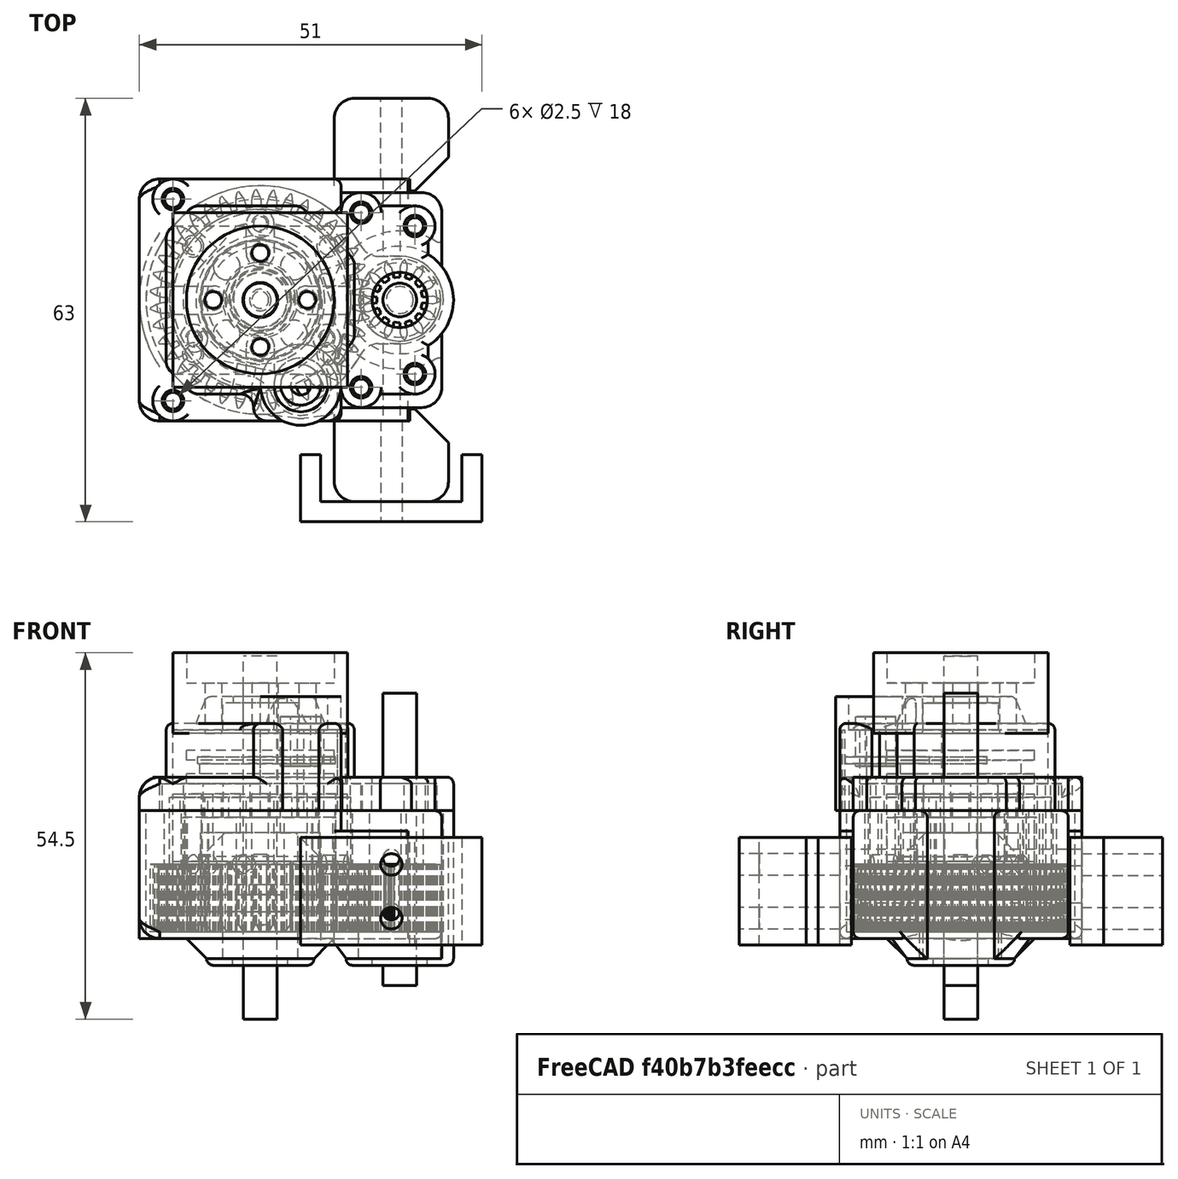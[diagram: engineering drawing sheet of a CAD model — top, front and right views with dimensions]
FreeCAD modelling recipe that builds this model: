
FCSTD DOCUMENT  (FreeCAD 0.16R6348 (Git))
Label: transfer-case
License: All rights reserved
LicenseURL: http://en.wikipedia.org/wiki/All_rights_reserved
objects: Part::Cylinder×134, Part::MultiFuse×79, Part::Feature×69, Part::Cut×42, Part::Box×25, Part::Fillet×23, Part::Chamfer×11, Part::Extrusion×3, Part::Mirroring×2, Part::Cone×2, Part::Part2DObjectPython×1, Part::Fuse×1, Part::FeaturePython×1
note: 393 computed .brp shape members not serialized (recipe doc carries the construction recipe); baked Part::Feature solids carry a one-line shape summary decoded from their .brp

FEATURE [Part::Cylinder] Cylinder
  Angle = 60
  Height = 7
  Placement = pos=(0,0,0) rot=(0,0,-1;0.20944rad)
  Radius = 11.5
FEATURE [Part::Cylinder] Cylinder001
  Angle = 60
  Height = 7
  Placement = pos=(0,0,0) rot=(0,0,1;3.97935rad)
  Radius = 11.5
FEATURE [Part::Cylinder] Cylinder002
  Angle = 60
  Height = 7
  Placement = pos=(0,0,0) rot=(0,0,1;1.88496rad)
  Radius = 11.5
FEATURE [Part::MultiFuse] Fusion
  Shapes = -> [Cylinder,Cylinder001,Cylinder002]
FEATURE [Part::Cylinder] Cylinder009
  Angle = 360
  Height = 10
  Placement = pos=(0,0,0) rot=(0,0,-1;0.20944rad)
  Radius = 13.5
FEATURE [Part::Cylinder] Cylinder010
  Angle = 360
  Height = 7
  Placement = pos=(0,0,0) rot=(0,0,-1;0.20944rad)
  Radius = 11.5
FEATURE [Part::Feature] Face
  shape: bbox 33.81 x 33.81 x 2e-07 mm, 1 faces, 0 solids (baked)
FEATURE [Part::Extrusion] Extrude
  Base = -> Face
  Dir = (0,0,7)
  Solid = false
FEATURE [Part::Cut] Cut
  Base = -> Fusion
  Tool = -> Extrude
FEATURE [Part::Cut] Cut001
  Base = -> Cylinder009
  Tool = -> Cylinder010
FEATURE [Part::Cylinder] Cylinder017
  Angle = 360
  Height = 20
  Radius = 4.7
FEATURE [Part::Cylinder] Cylinder018
  Angle = 360
  Height = 20
  Placement = pos=(0,0,-9) rot=(0,0,1;0rad)
  Radius = 1.4
FEATURE [Part::Cylinder] Cylinder019
  Angle = 360
  Height = 20
  Placement = pos=(0,0,-9) rot=(0,-1,0;2.0944rad)
  Radius = 1.4
FEATURE [Part::Cylinder] Cylinder020
  Angle = 360
  Height = 20
  Placement = pos=(0,0,-9) rot=(0,1,0;2.0944rad)
  Radius = 1.4
FEATURE [Part::MultiFuse] Fusion004
  Placement = pos=(-1.87121,-8.80333,0) rot=(0.989133,-0.103962,-0.103962;1.58172rad)
  Shapes = -> [Cylinder018,Cylinder019,Cylinder020]
FEATURE [Part::MultiFuse] Fusion005
  Shapes = -> [Cut,Cut001]
FEATURE [Part::Cut] Cut002
  Base = -> Fusion005
  Tool = -> Fusion004
FEATURE [Part::Cut] Cut003  label="hemi-box-01"
  Base = -> Cut002
  Tool = -> Cylinder017
FEATURE [Part::Cylinder] Cylinder021
  Angle = 360
  Height = 20
  Radius = 4.7
FEATURE [Part::Feature] Face001
  shape: bbox 33.81 x 33.81 x 2e-07 mm, 1 faces, 0 solids (baked)
FEATURE [Part::Extrusion] Extrude001
  Base = -> Face001
  Dir = (0,0,7)
  Solid = false
FEATURE [Part::Cylinder] Cylinder022
  Angle = 360
  Height = 20
  Placement = pos=(0,0,-9) rot=(0,0,1;0rad)
  Radius = 1.4
FEATURE [Part::Cylinder] Cylinder023
  Angle = 60
  Height = 7
  Placement = pos=(0,0,0) rot=(0,0,1;3.97935rad)
  Radius = 11.5
FEATURE [Part::Cylinder] Cylinder024
  Angle = 60
  Height = 7
  Placement = pos=(0,0,0) rot=(0,0,1;1.88496rad)
  Radius = 11.5
FEATURE [Part::Cylinder] Cylinder025
  Angle = 60
  Height = 7
  Placement = pos=(0,0,0) rot=(0,0,-1;0.20944rad)
  Radius = 11.5
FEATURE [Part::MultiFuse] Fusion007
  Shapes = -> [Cylinder025,Cylinder023,Cylinder024]
FEATURE [Part::Cut] Cut005
  Base = -> Fusion007
  Tool = -> Extrude001
FEATURE [Part::Cylinder] Cylinder026
  Angle = 360
  Height = 10
  Placement = pos=(0,0,0) rot=(0,0,-1;0.20944rad)
  Radius = 13.5
FEATURE [Part::Cylinder] Cylinder027
  Angle = 360
  Height = 7
  Placement = pos=(0,0,0) rot=(0,0,-1;0.20944rad)
  Radius = 11.5
FEATURE [Part::Cut] Cut006
  Base = -> Cylinder026
  Tool = -> Cylinder027
FEATURE [Part::MultiFuse] Fusion008
  Shapes = -> [Cut005,Cut006]
FEATURE [Part::Cylinder] Cylinder028
  Angle = 360
  Height = 20
  Placement = pos=(0,0,-9) rot=(0,-1,0;2.0944rad)
  Radius = 1.4
FEATURE [Part::Cylinder] Cylinder029
  Angle = 360
  Height = 20
  Placement = pos=(0,0,-9) rot=(0,1,0;2.0944rad)
  Radius = 1.4
FEATURE [Part::MultiFuse] Fusion006
  Placement = pos=(-1.87121,-8.80333,0) rot=(0.989133,-0.103962,-0.103962;1.58172rad)
  Shapes = -> [Cylinder022,Cylinder028,Cylinder029]
FEATURE [Part::Cut] Cut007
  Base = -> Fusion008
  Tool = -> Fusion006
FEATURE [Part::Cut] Cut004  label="hemi-box-01-copy"
  Base = -> Cut007
  Tool = -> Cylinder021
FEATURE [Part::Mirroring] Part__Mirroring  label="hemi-box-02"
  Base = (0,0,0)
  Normal = (0,0,1)
  Source = -> Cut004
FEATURE [Part::Feature] Cut014001  label="Cut015"
  Placement = pos=(0,0,-10) rot=(0,0,1;0rad)
  shape: bbox 32.76 x 32.78 x 10 mm, 549 faces (baked)
FEATURE [Part::Cylinder] Cylinder037
  Angle = 360
  Height = 10
  Placement = pos=(8.47185,-7.62809,0) rot=(0,0,-1;0.733038rad)
  Radius = 2.05
FEATURE [Part::Cylinder] Cylinder038
  Angle = 360
  Height = 10
  Placement = pos=(-10.842,-3.52279,0) rot=(0,0,1;3.45575rad)
  Radius = 2.05
FEATURE [Part::Cylinder] Cylinder039
  Angle = 360
  Height = 10
  Placement = pos=(2.37019,11.1509,0) rot=(0,0,1;1.36136rad)
  Radius = 2.05
FEATURE [Part::MultiFuse] Fusion014
  Placement = pos=(0,0,-10) rot=(0,0,1;0.20944rad)
  Shapes = -> [Cylinder037,Cylinder039,Cylinder038]
FEATURE [Part::Cylinder] Cylinder040
  Angle = 360
  Height = 10
  Placement = pos=(8.47185,-7.62809,0) rot=(0,0,-1;0.733038rad)
  Radius = 1.25
FEATURE [Part::Cylinder] Cylinder041
  Angle = 360
  Height = 10
  Placement = pos=(-10.842,-3.52279,0) rot=(0,0,1;3.45575rad)
  Radius = 1.25
FEATURE [Part::Cylinder] Cylinder042
  Angle = 360
  Height = 10
  Placement = pos=(2.37019,11.1509,0) rot=(0,0,1;1.36136rad)
  Radius = 1.25
FEATURE [Part::MultiFuse] Fusion015
  Placement = pos=(0,0,0) rot=(0,0,1;0.20944rad)
  Shapes = -> [Cylinder040,Cylinder042,Cylinder041]
FEATURE [Part::Cylinder] Cylinder043
  Angle = 360
  Height = 10
  Placement = pos=(8.47185,-7.62809,0) rot=(0,0,-1;0.733038rad)
  Radius = 2.05
FEATURE [Part::Cylinder] Cylinder044
  Angle = 360
  Height = 10
  Placement = pos=(-10.842,-3.52279,0) rot=(0,0,1;3.45575rad)
  Radius = 2.05
FEATURE [Part::Cylinder] Cylinder045
  Angle = 360
  Height = 10
  Placement = pos=(2.37019,11.1509,0) rot=(0,0,1;1.36136rad)
  Radius = 2.05
FEATURE [Part::MultiFuse] Fusion017
  Placement = pos=(0,0,0) rot=(0,0,1;0.20944rad)
  Shapes = -> [Cylinder043,Cylinder045,Cylinder044]
FEATURE [Part::Cylinder] Cylinder049
  Angle = 360
  Height = 10
  Placement = pos=(2.37019,11.1509,0) rot=(0,0,1;1.36136rad)
  Radius = 1
FEATURE [Part::Cylinder] Cylinder050
  Angle = 360
  Height = 10
  Placement = pos=(8.47185,-7.62809,0) rot=(0,0,-1;0.733038rad)
  Radius = 1
FEATURE [Part::Cylinder] Cylinder051
  Angle = 360
  Height = 10
  Placement = pos=(-10.842,-3.52279,0) rot=(0,0,1;3.45575rad)
  Radius = 1
FEATURE [Part::MultiFuse] Fusion020
  Placement = pos=(0,0,-9) rot=(0,0,1;0.20944rad)
  Shapes = -> [Cylinder050,Cylinder049,Cylinder051]
FEATURE [Part::MultiFuse] Fusion021
  Shapes = -> [Cut003,Fusion017]
FEATURE [Part::MultiFuse] Fusion022
  Shapes = -> [Fusion014,Part__Mirroring]
FEATURE [Part::MultiFuse] Fusion023
  Shapes = -> [Cut014001,Fusion022]
FEATURE [Part::Cut] Cut014008  label="diff-box-geared"
  Base = -> Fusion023
  Placement = pos=(0,0,-0.5) rot=(0,0,1;0rad)
  Tool = -> Fusion020
FEATURE [Part::Cylinder] Cylinder062
  Angle = 360
  Height = 2
  Placement = pos=(8.47185,-7.62809,0) rot=(0,0,-1;0.733038rad)
  Radius = 2.05
FEATURE [Part::Cylinder] Cylinder063
  Angle = 360
  Height = 2
  Placement = pos=(-10.842,-3.52279,0) rot=(0,0,1;3.45575rad)
  Radius = 2.05
FEATURE [Part::Cylinder] Cylinder064
  Angle = 360
  Height = 2
  Placement = pos=(2.37019,11.1509,0) rot=(0,0,1;1.36136rad)
  Radius = 2.05
FEATURE [Part::MultiFuse] Fusion030
  Placement = pos=(0,0,8) rot=(0,0,1;0.20944rad)
  Shapes = -> [Cylinder062,Cylinder064,Cylinder063]
FEATURE [Part::MultiFuse] Fusion031
  Shapes = -> [Fusion015,Fusion030]
FEATURE [Part::Cylinder] Cylinder065
  Angle = 360
  Height = 10
  Placement = pos=(7,0,0) rot=(0,0,1;0rad)
  Radius = 1.25
FEATURE [Part::Cylinder] Cylinder066
  Angle = 360
  Height = 10
  Placement = pos=(-7,0,0) rot=(0,0,1;0rad)
  Radius = 1.25
FEATURE [Part::MultiFuse] Fusion032
  Shapes = -> [Cylinder066,Cylinder065]
FEATURE [Part::Cylinder] Cylinder067
  Angle = 360
  Height = 10
  Placement = pos=(7,0,0) rot=(0,0,1;0rad)
  Radius = 1.25
FEATURE [Part::Cylinder] Cylinder068
  Angle = 360
  Height = 10
  Placement = pos=(-7,0,0) rot=(0,0,1;0rad)
  Radius = 1.25
FEATURE [Part::MultiFuse] Fusion033
  Placement = pos=(0,0,0) rot=(0,0,1;1.5708rad)
  Shapes = -> [Cylinder068,Cylinder067]
FEATURE [Part::MultiFuse] Fusion034
  Shapes = -> [Fusion033,Fusion032]
FEATURE [Part::Cut] Cut014009
  Base = -> Fusion021
  Tool = -> Fusion031
FEATURE [Part::Cut] Cut014010  label="diff-box-ungeared"
  Base = -> Cut014009
  Placement = pos=(0,0,-0.5) rot=(0,0,1;0rad)
  Tool = -> Fusion034
FEATURE [Part::Cylinder] Cylinder070
  Angle = 360
  Height = 4.2
  Radius = 8.9
FEATURE [Part::Cylinder] Cylinder072
  Angle = 360
  Height = 12
  Radius = 1.25
FEATURE [Part::MultiFuse] Fusion036
  Shapes = -> [Cylinder072,Cylinder070]
FEATURE [Part::Cylinder] Cylinder073
  Angle = 360
  Height = 15
  Placement = pos=(7,0,0) rot=(0,0,1;0rad)
  Radius = 2.1
FEATURE [Part::Cylinder] Cylinder074
  Angle = 360
  Height = 15
  Placement = pos=(-7,0,0) rot=(0,0,1;0rad)
  Radius = 2.1
FEATURE [Part::MultiFuse] Fusion037
  Shapes = -> [Cylinder074,Cylinder073]
FEATURE [Part::Cylinder] Cylinder075
  Angle = 360
  Height = 15
  Placement = pos=(7,0,0) rot=(0,0,1;0rad)
  Radius = 2.1
FEATURE [Part::Cylinder] Cylinder076
  Angle = 360
  Height = 15
  Placement = pos=(-7,0,0) rot=(0,0,1;0rad)
  Radius = 2.1
FEATURE [Part::MultiFuse] Fusion038
  Placement = pos=(0,0,0) rot=(0,0,1;1.5708rad)
  Shapes = -> [Cylinder076,Cylinder075]
FEATURE [Part::MultiFuse] Fusion039
  Placement = pos=(0,0,-3) rot=(0,0,1;0rad)
  Shapes = -> [Fusion038,Fusion037]
FEATURE [Part::Box] Box005  label="Cube005"
  Height = 10
  Length = 26
  Placement = pos=(-13,-11,0) rot=(0,0,1;0rad)
  Width = 22
FEATURE [Part::Cut] Cut014011
  Base = -> Box005
  Tool = -> Fusion036
FEATURE [Part::Cylinder] Cylinder077
  Angle = 360
  Height = 15
  Placement = pos=(7,0,0) rot=(0,0,1;0rad)
  Radius = 1.25
FEATURE [Part::Cylinder] Cylinder078
  Angle = 360
  Height = 15
  Placement = pos=(-7,0,0) rot=(0,0,1;0rad)
  Radius = 1.25
FEATURE [Part::Cylinder] Cylinder079
  Angle = 360
  Height = 4.5
  Radius = 11
FEATURE [Part::Cylinder] Cylinder080
  Angle = 360
  Height = 12
  Radius = 2.6
FEATURE [Part::MultiFuse] Fusion040
  Shapes = -> [Cylinder080,Cylinder079]
FEATURE [Part::Cylinder] Cylinder081
  Angle = 360
  Height = 15
  Placement = pos=(7,0,0) rot=(0,0,1;0rad)
  Radius = 1.25
FEATURE [Part::MultiFuse] Fusion042
  Shapes = -> [Cylinder078,Cylinder077]
FEATURE [Part::Box] Box006  label="Cube006"
  Height = 12
  Length = 26
  Placement = pos=(-13,-13,0) rot=(0,0,1;0rad)
  Width = 26
FEATURE [Part::Cut] Cut014014
  Base = -> Box006
  Tool = -> Fusion040
FEATURE [Part::Cylinder] Cylinder082
  Angle = 360
  Height = 15
  Placement = pos=(-7,0,0) rot=(0,0,1;0rad)
  Radius = 1.25
FEATURE [Part::MultiFuse] Fusion041
  Placement = pos=(0,0,0) rot=(0,0,1;1.5708rad)
  Shapes = -> [Cylinder082,Cylinder081]
FEATURE [Part::MultiFuse] Fusion043
  Placement = pos=(0,0,-3) rot=(0,0,1;0rad)
  Shapes = -> [Fusion041,Fusion042]
FEATURE [Part::Cut] Cut014015  label="diff_lock_HOLES"
  Base = -> Cut014014
  Placement = pos=(0,0,31) rot=(0,1,0;3.14159rad)
  Tool = -> Fusion043
FEATURE [Part::Box] Box  label="Cube"
  Height = 19
  Length = 15
  Placement = pos=(12,-16,-11.5) rot=(0,0,1;0rad)
  Width = 32
FEATURE [Part::Box] Box001  label="Cube001"
  Height = 19
  Length = 30
  Placement = pos=(-18,-18,-11.5) rot=(0,0,1;0rad)
  Width = 36
FEATURE [Part::Box] Box002  label="Cube002"
  Height = 16
  Length = 11
  Placement = pos=(11,-18,-11.5) rot=(0,0,1;0rad)
  Width = 36
FEATURE [Part::Box] Box003  label="Cube003"
  Height = 5
  Length = 14
  Placement = pos=(10,-14,6.5) rot=(0,0,1;0rad)
  Width = 28
FEATURE [Part::Fillet] Fillet001
  Base = -> Box003
  Edges = 2 edges r=3: [Edge5,Edge7]
FEATURE [Part::Fillet] Fillet002
  Base = -> Box
  Edges = 2 edges r=3: [Edge5,Edge7]
FEATURE [Part::Fillet] Fillet005
  Base = -> Fillet002
  Edges = 2 edges r=1: [Edge1,Edge4]
FEATURE [Part::Fillet] Fillet006
  Base = -> Fillet001
  Edges = 1 edges r=1: [Edge1]
  Placement = pos=(1,0,0) rot=(0,0,1;0rad)
FEATURE [Part::Part2DObjectPython] polygon  # Draft 2D object (typed FeaturePython)
  ChamferSize = 0
  DrawMode = 0
  FacesNumber = 26
  FilletRadius = 0
  MakeFace = true
  Placement = pos=(0,0,0) rot=(0,0,1;0.094388rad)
  Radius = 3.4
FEATURE [Part::Feature] wire
  shape: bbox 4.843 x 1.103 x 2e-07 mm, 1 faces, 0 solids (baked)
FEATURE [Part::Feature] wire001
  shape: bbox 5 x 1.103 x 2e-07 mm, 1 faces, 0 solids (baked)
FEATURE [Part::Feature] wire002
  shape: bbox 5.256 x 1.066 x 2e-07 mm, 1 faces, 0 solids (baked)
FEATURE [Part::Feature] wire003
  shape: bbox 5.595 x 0.9297 x 2e-07 mm, 1 faces, 0 solids (baked)
FEATURE [Part::Feature] wire004
  shape: bbox 6 x 0.6364 x 2e-07 mm, 1 faces, 0 solids (baked)
FEATURE [Part::MultiFuse] Group
  Placement = pos=(0,0,0) rot=(0,0,1;0.483322rad)
  Shapes = -> [wire,wire001,wire002,wire003,wire004]
FEATURE [Part::Feature] wire005
  shape: bbox 4.843 x 1.103 x 2e-07 mm, 1 faces, 0 solids (baked)
FEATURE [Part::Feature] wire006
  shape: bbox 5 x 1.103 x 2e-07 mm, 1 faces, 0 solids (baked)
FEATURE [Part::Feature] wire007
  shape: bbox 5.256 x 1.066 x 2e-07 mm, 1 faces, 0 solids (baked)
FEATURE [Part::Feature] wire008
  shape: bbox 5.595 x 0.9297 x 2e-07 mm, 1 faces, 0 solids (baked)
FEATURE [Part::Feature] wire009
  shape: bbox 6 x 0.6364 x 2e-07 mm, 1 faces, 0 solids (baked)
FEATURE [Part::MultiFuse] Group001
  Placement = pos=(0,0,0) rot=(0,0,1;0.966644rad)
  Shapes = -> [wire005,wire006,wire007,wire008,wire009]
FEATURE [Part::Feature] wire010
  shape: bbox 4.843 x 1.103 x 2e-07 mm, 1 faces, 0 solids (baked)
FEATURE [Part::Feature] wire011
  shape: bbox 5 x 1.103 x 2e-07 mm, 1 faces, 0 solids (baked)
FEATURE [Part::Feature] wire012
  shape: bbox 5.256 x 1.066 x 2e-07 mm, 1 faces, 0 solids (baked)
FEATURE [Part::Feature] wire013
  shape: bbox 5.595 x 0.9297 x 2e-07 mm, 1 faces, 0 solids (baked)
FEATURE [Part::Feature] wire014
  shape: bbox 6 x 0.6364 x 2e-07 mm, 1 faces, 0 solids (baked)
FEATURE [Part::MultiFuse] Group002
  Placement = pos=(0,0,0) rot=(0,0,1;1.44997rad)
  Shapes = -> [wire010,wire011,wire012,wire013,wire014]
FEATURE [Part::Feature] wire015
  shape: bbox 4.843 x 1.103 x 2e-07 mm, 1 faces, 0 solids (baked)
FEATURE [Part::Feature] wire016
  shape: bbox 5 x 1.103 x 2e-07 mm, 1 faces, 0 solids (baked)
FEATURE [Part::Feature] wire017
  shape: bbox 5.256 x 1.066 x 2e-07 mm, 1 faces, 0 solids (baked)
FEATURE [Part::Feature] wire018
  shape: bbox 5.595 x 0.9297 x 2e-07 mm, 1 faces, 0 solids (baked)
FEATURE [Part::Feature] wire019
  shape: bbox 6 x 0.6364 x 2e-07 mm, 1 faces, 0 solids (baked)
FEATURE [Part::MultiFuse] Group003
  Placement = pos=(0,0,0) rot=(0,0,1;1.93329rad)
  Shapes = -> [wire015,wire016,wire017,wire018,wire019]
FEATURE [Part::Feature] wire020
  shape: bbox 4.843 x 1.103 x 2e-07 mm, 1 faces, 0 solids (baked)
FEATURE [Part::Feature] wire021
  shape: bbox 5 x 1.103 x 2e-07 mm, 1 faces, 0 solids (baked)
FEATURE [Part::Feature] wire022
  shape: bbox 5.256 x 1.066 x 2e-07 mm, 1 faces, 0 solids (baked)
FEATURE [Part::Feature] wire023
  shape: bbox 5.595 x 0.9297 x 2e-07 mm, 1 faces, 0 solids (baked)
FEATURE [Part::Feature] wire024
  shape: bbox 6 x 0.6364 x 2e-07 mm, 1 faces, 0 solids (baked)
FEATURE [Part::MultiFuse] Group004
  Placement = pos=(0,0,0) rot=(0,0,1;2.41661rad)
  Shapes = -> [wire020,wire021,wire022,wire023,wire024]
FEATURE [Part::Feature] wire025
  shape: bbox 4.843 x 1.103 x 2e-07 mm, 1 faces, 0 solids (baked)
FEATURE [Part::Feature] wire026
  shape: bbox 5 x 1.103 x 2e-07 mm, 1 faces, 0 solids (baked)
FEATURE [Part::Feature] wire027
  shape: bbox 5.256 x 1.066 x 2e-07 mm, 1 faces, 0 solids (baked)
FEATURE [Part::Feature] wire028
  shape: bbox 5.595 x 0.9297 x 2e-07 mm, 1 faces, 0 solids (baked)
FEATURE [Part::Feature] wire029
  shape: bbox 6 x 0.6364 x 2e-07 mm, 1 faces, 0 solids (baked)
FEATURE [Part::MultiFuse] Group005
  Placement = pos=(0,0,0) rot=(0,0,1;2.89993rad)
  Shapes = -> [wire025,wire026,wire027,wire028,wire029]
FEATURE [Part::Feature] wire030
  shape: bbox 4.843 x 1.103 x 2e-07 mm, 1 faces, 0 solids (baked)
FEATURE [Part::Feature] wire031
  shape: bbox 5 x 1.103 x 2e-07 mm, 1 faces, 0 solids (baked)
FEATURE [Part::Feature] wire032
  shape: bbox 5.256 x 1.066 x 2e-07 mm, 1 faces, 0 solids (baked)
FEATURE [Part::Feature] wire033
  shape: bbox 5.595 x 0.9297 x 2e-07 mm, 1 faces, 0 solids (baked)
FEATURE [Part::Feature] wire034
  shape: bbox 6 x 0.6364 x 2e-07 mm, 1 faces, 0 solids (baked)
FEATURE [Part::MultiFuse] Group006
  Placement = pos=(0,0,0) rot=(0,0,1;3.38325rad)
  Shapes = -> [wire030,wire031,wire032,wire033,wire034]
FEATURE [Part::Feature] wire035
  shape: bbox 4.843 x 1.103 x 2e-07 mm, 1 faces, 0 solids (baked)
FEATURE [Part::Feature] wire036
  shape: bbox 5 x 1.103 x 2e-07 mm, 1 faces, 0 solids (baked)
FEATURE [Part::Feature] wire037
  shape: bbox 5.256 x 1.066 x 2e-07 mm, 1 faces, 0 solids (baked)
FEATURE [Part::Feature] wire038
  shape: bbox 5.595 x 0.9297 x 2e-07 mm, 1 faces, 0 solids (baked)
FEATURE [Part::Feature] wire039
  shape: bbox 6 x 0.6364 x 2e-07 mm, 1 faces, 0 solids (baked)
FEATURE [Part::MultiFuse] Group007
  Placement = pos=(0,0,0) rot=(0,0,1;3.86658rad)
  Shapes = -> [wire035,wire036,wire037,wire038,wire039]
FEATURE [Part::Feature] wire040
  shape: bbox 4.843 x 1.103 x 2e-07 mm, 1 faces, 0 solids (baked)
FEATURE [Part::Feature] wire041
  shape: bbox 5 x 1.103 x 2e-07 mm, 1 faces, 0 solids (baked)
FEATURE [Part::Feature] wire042
  shape: bbox 5.256 x 1.066 x 2e-07 mm, 1 faces, 0 solids (baked)
FEATURE [Part::Feature] wire043
  shape: bbox 5.595 x 0.9297 x 2e-07 mm, 1 faces, 0 solids (baked)
FEATURE [Part::Feature] wire044
  shape: bbox 6 x 0.6364 x 2e-07 mm, 1 faces, 0 solids (baked)
FEATURE [Part::MultiFuse] Group008
  Placement = pos=(0,0,0) rot=(0,0,-1;1.93329rad)
  Shapes = -> [wire040,wire041,wire042,wire043,wire044]
FEATURE [Part::Feature] wire045
  shape: bbox 4.843 x 1.103 x 2e-07 mm, 1 faces, 0 solids (baked)
FEATURE [Part::Feature] wire046
  shape: bbox 5 x 1.103 x 2e-07 mm, 1 faces, 0 solids (baked)
FEATURE [Part::Feature] wire047
  shape: bbox 5.256 x 1.066 x 2e-07 mm, 1 faces, 0 solids (baked)
FEATURE [Part::Feature] wire048
  shape: bbox 5.595 x 0.9297 x 2e-07 mm, 1 faces, 0 solids (baked)
FEATURE [Part::Feature] wire049
  shape: bbox 6 x 0.6364 x 2e-07 mm, 1 faces, 0 solids (baked)
FEATURE [Part::MultiFuse] Group009
  Placement = pos=(0,0,0) rot=(0,0,-1;1.44997rad)
  Shapes = -> [wire045,wire046,wire047,wire048,wire049]
FEATURE [Part::Feature] wire050
  shape: bbox 4.843 x 1.103 x 2e-07 mm, 1 faces, 0 solids (baked)
FEATURE [Part::Feature] wire051
  shape: bbox 5 x 1.103 x 2e-07 mm, 1 faces, 0 solids (baked)
FEATURE [Part::Feature] wire052
  shape: bbox 5.256 x 1.066 x 2e-07 mm, 1 faces, 0 solids (baked)
FEATURE [Part::Feature] wire053
  shape: bbox 5.595 x 0.9297 x 2e-07 mm, 1 faces, 0 solids (baked)
FEATURE [Part::Feature] wire054
  shape: bbox 6 x 0.6364 x 2e-07 mm, 1 faces, 0 solids (baked)
FEATURE [Part::MultiFuse] Group010
  Placement = pos=(0,0,0) rot=(0,0,-1;0.966644rad)
  Shapes = -> [wire050,wire051,wire052,wire053,wire054]
FEATURE [Part::Feature] wire055
  shape: bbox 4.843 x 1.103 x 2e-07 mm, 1 faces, 0 solids (baked)
FEATURE [Part::Feature] wire056
  shape: bbox 5 x 1.103 x 2e-07 mm, 1 faces, 0 solids (baked)
FEATURE [Part::Feature] wire057
  shape: bbox 5.256 x 1.066 x 2e-07 mm, 1 faces, 0 solids (baked)
FEATURE [Part::Feature] wire058
  shape: bbox 5.595 x 0.9297 x 2e-07 mm, 1 faces, 0 solids (baked)
FEATURE [Part::Feature] wire059
  shape: bbox 6 x 0.6364 x 2e-07 mm, 1 faces, 0 solids (baked)
FEATURE [Part::MultiFuse] Group011
  Placement = pos=(0,0,0) rot=(0,0,-1;0.483322rad)
  Shapes = -> [wire055,wire056,wire057,wire058,wire059]
FEATURE [Part::Feature] wire060
  shape: bbox 4.843 x 1.103 x 2e-07 mm, 1 faces, 0 solids (baked)
FEATURE [Part::Feature] wire061
  shape: bbox 5 x 1.103 x 2e-07 mm, 1 faces, 0 solids (baked)
FEATURE [Part::Feature] wire062
  shape: bbox 5.256 x 1.066 x 2e-07 mm, 1 faces, 0 solids (baked)
FEATURE [Part::Feature] wire063
  shape: bbox 5.595 x 0.9297 x 2e-07 mm, 1 faces, 0 solids (baked)
FEATURE [Part::Feature] wire064
  shape: bbox 6 x 0.6364 x 2e-07 mm, 1 faces, 0 solids (baked)
FEATURE [Part::MultiFuse] Group012
  Shapes = -> [wire060,wire061,wire062,wire063,wire064]
FEATURE [Part::MultiFuse] Group013
  Shapes = -> [Group,Group001,Group002,Group003,Group004,Group005,Group006,Group007,Group008,Group009,Group010,Group011,Group012]
FEATURE [Part::Fuse] union
  Base = -> polygon
  Tool = -> Group013
FEATURE [Part::FeaturePython] RefineLinearExtrude  # WARN: FeaturePython — macro-defined, semantics opaque (R4)
  Base = -> union
FEATURE [Part::Extrusion] LinearExtrude
  Base = -> RefineLinearExtrude
  Dir = (0,0,10)
  Solid = true
FEATURE [Part::Feature] emptycyl
  Placement = pos=(0,0,-1) rot=(0,0,1;0rad)
FEATURE [Part::Cut] difference
  Base = -> LinearExtrude
  Tool = -> emptycyl
FEATURE [Part::Cylinder] Cylinder083
  Angle = 360
  Height = 10
  Radius = 2
FEATURE [Part::Cut] Cut014016  label="gear-13T"
  Base = -> difference
  Placement = pos=(20.75,0,-10.5) rot=(0,0,1;0rad)
  Tool = -> Cylinder083
FEATURE [Part::Cylinder] Cylinder084
  Angle = 360
  Height = 4
  Placement = pos=(0,0,-14.5) rot=(0,0,1;0rad)
  Radius = 5.6
FEATURE [Part::Cylinder] Cylinder085
  Angle = 360
  Height = 4
  Placement = pos=(20.75,0,-14.5) rot=(0,0,1;0rad)
  Radius = 6.1
FEATURE [Part::Cylinder] Cylinder086
  Angle = 360
  Height = 21
  Placement = pos=(20.75,0,-10.5) rot=(0,0,1;0rad)
  Radius = 6.5
FEATURE [Part::Cylinder] Cylinder087
  Angle = 360
  Height = 54
  Placement = pos=(0,0,-23.5) rot=(0,0,1;0rad)
  Radius = 2.5
FEATURE [Part::Cylinder] Cylinder088
  Angle = 360
  Height = 43.5
  Placement = pos=(20.75,0,-18.5) rot=(0,0,1;0rad)
  Radius = 2.5
FEATURE [Part::Cylinder] Cylinder089
  Angle = 360
  Height = 7
  Placement = pos=(0,0,10.5) rot=(0,0,1;0rad)
  Radius = 10.5
FEATURE [Part::Fillet] Fillet
  Base = -> Box001
  Edges = 5 edges r=1: [Edge5,Edge7,Edge8,Edge9,Edge11]
FEATURE [Part::Fillet] Fillet009
  Base = -> Fillet
  Edges = 3 edges r=3: [Edge1,Edge4,Edge5]
FEATURE [Part::Box] Box007  label="Cube007"
  Height = 5
  Length = 30
  Placement = pos=(-18,-18,6.5) rot=(0,0,1;0rad)
  Width = 36
FEATURE [Part::Fillet] Fillet010
  Base = -> Box007
  Edges = 5 edges r=1: [Edge5,Edge6,Edge7,Edge10,Edge12]
FEATURE [Part::Fillet] Fillet011
  Base = -> Fillet010
  Edges = 3 edges r=3: [Edge1,Edge4,Edge5]
FEATURE [Part::Cylinder] Cylinder090
  Angle = 360
  Height = 21
  Placement = pos=(0,0,-10.5) rot=(0,0,1;0rad)
  Radius = 17
FEATURE [Part::Cylinder] Cylinder092
  Angle = 360
  Height = 23
  Placement = pos=(20.75,0,-15.5) rot=(0,0,1;0rad)
  Radius = 8
FEATURE [Part::Cylinder] Cylinder094
  Angle = 360
  Height = 4
  Placement = pos=(0,0,-15.5) rot=(0,0,1;0rad)
  Radius = 8
FEATURE [Part::Cylinder] Cylinder097
  Angle = 360
  Height = 45
  Placement = pos=(0,0,-19.5) rot=(0,0,1;0rad)
  Radius = 4.1
FEATURE [Part::Cylinder] Cylinder098
  Angle = 360
  Height = 18
  Placement = pos=(-13,15,-11.5) rot=(0,0,1;0rad)
  Radius = 1.25
FEATURE [Part::Cylinder] Cylinder099
  Angle = 360
  Height = 18
  Placement = pos=(-13,-15,-11.5) rot=(0,0,1;0rad)
  Radius = 1.25
FEATURE [Part::Cylinder] Cylinder100
  Angle = 360
  Height = 18
  Placement = pos=(15,13,-11.5) rot=(0,0,1;0rad)
  Radius = 1.25
FEATURE [Part::Cylinder] Cylinder101
  Angle = 360
  Height = 18
  Placement = pos=(15,-13,-11.5) rot=(0,0,1;0rad)
  Radius = 1.25
FEATURE [Part::Cylinder] Cylinder102
  Angle = 360
  Height = 18
  Placement = pos=(23,11,-11.5) rot=(0,0,1;0rad)
  Radius = 1.25
FEATURE [Part::Cylinder] Cylinder103
  Angle = 360
  Height = 18
  Placement = pos=(23,-11,-11.5) rot=(0,0,1;0rad)
  Radius = 1.25
FEATURE [Part::MultiFuse] Fusion052
  Placement = pos=(0,0,1) rot=(0,0,1;0rad)
  Shapes = -> [Cylinder098,Cylinder099,Cylinder102,Cylinder100,Cylinder103,Cylinder101]
FEATURE [Part::Cylinder] Cylinder105
  Angle = 360
  Height = 5
  Placement = pos=(20,0,-15.5) rot=(0,0,1;0rad)
  Radius = 8
FEATURE [Part::Cone] Cone001
  Angle = 360
  Height = 4
  Placement = pos=(20,0,-14.5) rot=(0,0,1;0rad)
  Radius1 = 8
  Radius2 = 11
FEATURE [Part::Box] Box008  label="Cube008"
  Height = 10
  Length = 10
  Placement = pos=(26.25,-13,-19) rot=(0,0,1;0rad)
  Width = 26
FEATURE [Part::MultiFuse] Fusion053
  Shapes = -> [Cylinder105,Box008]
FEATURE [Part::Cut] Cut014019
  Base = -> Cone001
  Placement = pos=(0.75,0,0) rot=(0,0,1;0rad)
  Tool = -> Fusion053
FEATURE [Part::Cylinder] Cylinder897  label="Cylinder1020"
  Angle = 360
  Height = 20
  Placement = pos=(19.5,30,-7.5) rot=(1,0,0;1.5708rad)
  Radius = 1.6
FEATURE [Part::Cylinder] Cylinder898  label="Cylinder1021"
  Angle = 360
  Height = 20
  Placement = pos=(19.5,30,0.5) rot=(1,0,0;1.5708rad)
  Radius = 1.6
FEATURE [Part::Box] Box552  label="Cube743"
  Height = 16
  Length = 17
  Placement = pos=(11,-30,-11.5) rot=(0,0,1;0rad)
  Width = 12
FEATURE [Part::Box] Box553  label="Cube744"
  Height = 16
  Length = 5.75
  Placement = pos=(22.25,-18,-11.5) rot=(0,0,1;0rad)
  Width = 1.75
FEATURE [Part::MultiFuse] Fusion055
  Shapes = -> [Box553,Box552]
FEATURE [Part::Chamfer] Chamfer001
  Base = -> Fusion055
  Edges = 1 edges r=5: [Edge2]
FEATURE [Part::Fillet] Fillet013
  Base = -> Chamfer001
  Edges = 2 edges r=3: [Edge19,Edge21]
FEATURE [Part::MultiFuse] Fusion056
  Placement = pos=(0,-40,0) rot=(0,0,1;0rad)
  Shapes = -> [Cylinder897,Cylinder898]
FEATURE [Part::Cut] Cut014020  label="diff-box-mount-left"
  Base = -> Fillet013
  Placement = pos=(0,0,-1) rot=(0,0,1;0rad)
  Tool = -> Fusion056
FEATURE [Part::Cylinder] Cylinder899  label="Cylinder1022"
  Angle = 360
  Height = 40
  Placement = pos=(19.5,30,-7.5) rot=(1,0,0;1.5708rad)
  Radius = 1.25
FEATURE [Part::Cylinder] Cylinder900  label="Cylinder1023"
  Angle = 360
  Height = 40
  Placement = pos=(19.5,30,0.5) rot=(1,0,0;1.5708rad)
  Radius = 1.25
FEATURE [Part::Box] Box554  label="Cube745"
  Height = 16
  Length = 17
  Placement = pos=(11,-30,-11.5) rot=(0,0,1;0rad)
  Width = 12
FEATURE [Part::Box] Box555  label="Cube746"
  Height = 16
  Length = 5.75
  Placement = pos=(22.25,-18,-11.5) rot=(0,0,1;0rad)
  Width = 1.75
FEATURE [Part::MultiFuse] Fusion058
  Shapes = -> [Box555,Box554]
FEATURE [Part::Chamfer] Chamfer002
  Base = -> Fusion058
  Edges = 1 edges r=5: [Edge2]
FEATURE [Part::Fillet] Fillet014
  Base = -> Chamfer002
  Edges = 2 edges r=3: [Edge19,Edge21]
FEATURE [Part::Cylinder] Cylinder901  label="Cylinder1024"
  Angle = 360
  Height = 20
  Placement = pos=(19.5,30,0.5) rot=(1,0,0;1.5708rad)
  Radius = 1.6
FEATURE [Part::Cylinder] Cylinder902  label="Cylinder1025"
  Angle = 360
  Height = 20
  Placement = pos=(19.5,30,-7.5) rot=(1,0,0;1.5708rad)
  Radius = 1.6
FEATURE [Part::MultiFuse] Fusion059
  Placement = pos=(0,-40,0) rot=(0,0,1;0rad)
  Shapes = -> [Cylinder902,Cylinder901]
FEATURE [Part::Cut] Cut014022
  Base = -> Fillet014
  Tool = -> Fusion059
FEATURE [Part::Mirroring] Part__Mirroring001  label="diff-box-mount-right"
  Base = (0,0,0)
  Normal = (0,1,0)
  Placement = pos=(0,0,-1) rot=(0,0,1;0rad)
  Source = -> Cut014022
FEATURE [Part::Cylinder] Cylinder903  label="Cylinder1026"
  Angle = 180
  Height = 1
  Radius = 9
FEATURE [Part::Cylinder] Cylinder904  label="Cylinder1027"
  Angle = 180
  Height = 1
  Radius = 11
FEATURE [Part::Cylinder] Cylinder905  label="Cylinder1028"
  Angle = 360
  Height = 1
  Placement = pos=(0,13.5,0) rot=(0,0,1;0rad)
  Radius = 4.5
FEATURE [Part::Cut] Cut014023
  Base = -> Cylinder904
  Tool = -> Cylinder903
FEATURE [Part::Cylinder] Cylinder906  label="Cylinder1029"
  Angle = 360
  Height = 7.35
  Placement = pos=(0,13.5,-0.35) rot=(0,0,1;0rad)
  Radius = 3
FEATURE [Part::Cylinder] Cylinder907  label="Cylinder1030"
  Angle = 360
  Height = 7.35
  Placement = pos=(0,13.5,-0.35) rot=(0,0,1;0rad)
  Radius = 1.5
FEATURE [Part::MultiFuse] Fusion060
  Shapes = -> [Cylinder905,Cut014023,Cylinder906]
FEATURE [Part::Cut] Cut014024
  Base = -> Fusion060
  Tool = -> Cylinder907
FEATURE [Part::Fillet] Fillet015
  Base = -> Cut014024
  Edges = 2 edges r=5: [Edge4,Edge26]
FEATURE [Part::Fillet] Fillet016  label="selector"
  Base = -> Fillet015
  Edges = 4 edges r=0.99: [Edge3,Edge20,Edge33,Edge34]
  Placement = pos=(0.213923,-0.468228,14.5) rot=(0,0,1;3.58665rad)
FEATURE [Part::Cylinder] Cylinder908
  Angle = 360
  Height = 2
  Placement = pos=(0,0,13.5) rot=(0,0,1;0rad)
  Radius = 9
FEATURE [Part::Cylinder] Cylinder909
  Angle = 360
  Height = 1.5
  Placement = pos=(0,0,15.5) rot=(0,0,1;0rad)
  Radius = 11
FEATURE [Part::Cylinder] Cylinder910
  Angle = 360
  Height = 1.5
  Placement = pos=(0,0,12) rot=(0,0,1;0rad)
  Radius = 11
FEATURE [Part::Cylinder] Cylinder911
  Angle = 360
  Height = 13
  Placement = pos=(0,0,-2.5) rot=(0,0,1;0rad)
  Radius = 15
FEATURE [Part::Cylinder] Cylinder912
  Angle = 360
  Height = 8
  Placement = pos=(0,0,10.5) rot=(0,0,1;0rad)
  Radius = 13
FEATURE [Part::Cylinder] Cylinder913
  Angle = 360
  Height = 5
  Placement = pos=(7,0,0) rot=(0,0,1;0rad)
  Radius = 1.5
FEATURE [Part::Cylinder] Cylinder914
  Angle = 360
  Height = 5
  Placement = pos=(-7,0,0) rot=(0,0,1;0rad)
  Radius = 1.5
FEATURE [Part::MultiFuse] Fusion063
  Shapes = -> [Cylinder914,Cylinder913]
FEATURE [Part::Cylinder] Cylinder915
  Angle = 360
  Height = 5
  Placement = pos=(7,0,0) rot=(0,0,1;0rad)
  Radius = 1.5
FEATURE [Part::Cylinder] Cylinder916
  Angle = 360
  Height = 5
  Placement = pos=(-7,0,0) rot=(0,0,1;0rad)
  Radius = 1.5
FEATURE [Part::MultiFuse] Fusion064
  Placement = pos=(0,0,0) rot=(0,0,1;1.5708rad)
  Shapes = -> [Cylinder916,Cylinder915]
FEATURE [Part::MultiFuse] Fusion065
  Placement = pos=(0,0,8) rot=(0,0,1;0rad)
  Shapes = -> [Fusion064,Fusion063]
FEATURE [Part::Cylinder] Cylinder917
  Angle = 360
  Height = 14
  Placement = pos=(-13,15,-11.5) rot=(0,0,1;0rad)
  Radius = 1.6
FEATURE [Part::Cylinder] Cylinder918
  Angle = 360
  Height = 14
  Placement = pos=(-13,-15,-11.5) rot=(0,0,1;0rad)
  Radius = 1.6
FEATURE [Part::Cylinder] Cylinder919
  Angle = 360
  Height = 14
  Placement = pos=(15,13,-11.5) rot=(0,0,1;0rad)
  Radius = 1.6
FEATURE [Part::Cylinder] Cylinder920
  Angle = 360
  Height = 14
  Placement = pos=(15,-13,-11.5) rot=(0,0,1;0rad)
  Radius = 1.6
FEATURE [Part::Cylinder] Cylinder921
  Angle = 360
  Height = 14
  Placement = pos=(23,11,-11.5) rot=(0,0,1;0rad)
  Radius = 1.6
FEATURE [Part::Cylinder] Cylinder922
  Angle = 360
  Height = 14
  Placement = pos=(23,-11,-11.5) rot=(0,0,1;0rad)
  Radius = 1.6
FEATURE [Part::MultiFuse] Fusion067
  Placement = pos=(0,0,9) rot=(0,0,1;0rad)
  Shapes = -> [Cylinder917,Cylinder918,Cylinder921,Cylinder919,Cylinder922,Cylinder920]
FEATURE [Part::MultiFuse] Fusion072
  Placement = pos=(0,0,1) rot=(0,0,1;0rad)
  Shapes = -> [Cylinder908,Cylinder909,Cylinder910]
FEATURE [Part::MultiFuse] Fusion073  label="selector-gear"
  Placement = pos=(0,0,-1.5) rot=(0,0,1;0rad)
  Shapes = -> [Fusion072,Fusion065]
FEATURE [Part::Box] Box556  label="Cube747"
  Height = 9
  Length = 13
  Placement = pos=(-1,-17,10.5) rot=(0,0,1;0rad)
  Width = 11
FEATURE [Part::Fillet] Fillet017
  Base = -> Box556
  Edges = 2 edges r=2: [Edge1,Edge5]
FEATURE [Part::Fillet] Fillet018
  Base = -> Fillet017
  Edges = 5 edges r=1: [Edge1,Edge5,Edge7,Edge8,Edge9]
  Placement = pos=(0,-1,0) rot=(0,0,1;0rad)
FEATURE [Part::Box] Box557  label="Cube748"
  Height = 13
  Length = 11.5
  Placement = pos=(0,-16.5,5.5) rot=(0,0,1;0rad)
  Width = 17
FEATURE [Part::Fillet] Fillet019
  Base = -> Box557
  Edges = 2 edges r=2: [Edge1,Edge5]
  Placement = pos=(0,-0.75,0) rot=(0,0,1;0rad)
FEATURE [Part::Cylinder] Cylinder931  label="Cylinder1031"
  Angle = 360
  Height = 5
  Placement = pos=(6.02716,-12.6362,18.5) rot=(0,0,1;0.445059rad)
  Radius = 4.5
FEATURE [Part::Cylinder] Cylinder932  label="Cylinder1032"
  Angle = 360
  Height = 17
  Placement = pos=(7,-12.1244,6.5) rot=(0,0,1;0.523599rad)
  Radius = 4
FEATURE [Part::Cylinder] Cylinder933  label="Cylinder1033"
  Angle = 360
  Height = 17
  Placement = pos=(7,-12.1244,6.5) rot=(0,0,1;0.523599rad)
  Radius = 6
FEATURE [Part::Box] Box558  label="Cube749"
  Height = 9
  Length = 28
  Placement = pos=(-14,-14,10.5) rot=(0,0,1;0rad)
  Width = 28
FEATURE [Part::Chamfer] Chamfer003
  Base = -> Box558
  Edges = 2 edges r=8: [Edge5,Edge7]
FEATURE [Part::Chamfer] Chamfer004
  Base = -> Chamfer003
  Edges = 2 edges r=4: [Edge17,Edge18]
FEATURE [Part::Fillet] Fillet020
  Base = -> Chamfer004
  Edges = 8 edges r=2: [Edge10,Edge11,Edge13,Edge15,Edge16,Edge18,Edge21,Edge23]
FEATURE [Part::Fillet] Fillet021
  Base = -> Fillet020
  Edges = 8 edges r=1: [Edge1,Edge4,Edge5,Edge8,Edge9,Edge12,Edge13,Edge16]
FEATURE [Part::Cut] Cut014027
  Base = -> Cylinder933
  Placement = pos=(0,0,0) rot=(0,0,-1;0.07854rad)
  Tool = -> Cylinder932
FEATURE [Part::Cylinder] Cylinder934
  Angle = 360
  Height = 5
  Placement = pos=(20.75,0,6.5) rot=(0,0,1;0rad)
  Radius = 8
FEATURE [Part::Cylinder] Cylinder935
  Angle = 360
  Height = 4
  Placement = pos=(20.75,0,6.5) rot=(0,0,1;0rad)
  Radius = 5.55
FEATURE [Part::Fillet] Fillet022
  Base = -> Cylinder934
  Edges = 1 edges r=1: [Edge1]
FEATURE [Part::Cylinder] Cylinder936
  Angle = 360
  Height = 34
  Placement = pos=(20.75,0,-14.5) rot=(0,0,1;0rad)
  Radius = 4.1
FEATURE [Part::Cylinder] Cylinder937
  Angle = 360
  Height = 10
  Placement = pos=(0,0,0.5) rot=(0,0,1;0rad)
  Radius = 14
FEATURE [Part::Cylinder] Cylinder940
  Angle = 360
  Height = 4
  Placement = pos=(0,0,18.5) rot=(0,0,1;0rad)
  Radius = 5.6
FEATURE [Part::Cone] Cone
  Angle = 360
  Height = 5
  Placement = pos=(0,0,18.5) rot=(0,0,1;0rad)
  Radius1 = 10
  Radius2 = 8
FEATURE [Part::Fillet] Fillet023
  Base = -> Cone
  Edges = 1 edges r=1: [Edge1]
FEATURE [Part::Cylinder] Cylinder941
  Angle = 360
  Height = 45
  Placement = pos=(0,0,-19.5) rot=(0,0,1;0rad)
  Radius = 4
FEATURE [Part::MultiFuse] Fusion083
  Shapes = -> [Cylinder937,Cylinder935,Cylinder936]
FEATURE [Part::MultiFuse] Fusion085
  Shapes = -> [Cylinder940,Cylinder941]
FEATURE [Part::MultiFuse] Fusion086
  Placement = pos=(0,-10,0) rot=(0,0,1;0rad)
  Shapes = -> [Cylinder899,Cylinder900]
FEATURE [Part::Cylinder] Cylinder944
  Angle = 360
  Height = 45
  Placement = pos=(20.75,0,-19.5) rot=(0,0,1;0rad)
  Radius = 4.1
FEATURE [Part::Cylinder] Cylinder945
  Angle = 360
  Height = 5
  Placement = pos=(-13,15,-11.5) rot=(0,0,1;0rad)
  Radius = 3
FEATURE [Part::Cylinder] Cylinder946
  Angle = 360
  Height = 5
  Placement = pos=(-13,-15,-11.5) rot=(0,0,1;0rad)
  Radius = 3
FEATURE [Part::Cylinder] Cylinder947
  Angle = 360
  Height = 5
  Placement = pos=(15,13,-11.5) rot=(0,0,1;0rad)
  Radius = 3
FEATURE [Part::Cylinder] Cylinder948
  Angle = 360
  Height = 5
  Placement = pos=(15,-13,-11.5) rot=(0,0,1;0rad)
  Radius = 3
FEATURE [Part::Cylinder] Cylinder949
  Angle = 360
  Height = 5
  Placement = pos=(23,11,-11.5) rot=(0,0,1;0rad)
  Radius = 3
FEATURE [Part::Cylinder] Cylinder950
  Angle = 360
  Height = 5
  Placement = pos=(23,-11,-11.5) rot=(0,0,1;0rad)
  Radius = 3
FEATURE [Part::MultiFuse] Fusion091
  Placement = pos=(0,0,18) rot=(0,0,1;0rad)
  Shapes = -> [Cylinder945,Cylinder946,Cylinder949,Cylinder947,Cylinder950,Cylinder948]
FEATURE [Part::MultiFuse] Fusion092
  Shapes = -> [Fillet019,Cylinder911,Cylinder912]
FEATURE [Part::MultiFuse] Fusion093
  Shapes = -> [Fillet018,Fillet006,Fillet011,Fillet021]
FEATURE [Part::Cylinder] Cylinder951  label="Cylinder1034"
  Angle = 360
  Height = 13
  Placement = pos=(6.02716,-12.6362,5.5) rot=(0,0,1;0.445059rad)
  Radius = 5
FEATURE [Part::Cut] Cut014036
  Base = -> Fusion093
  Tool = -> Cylinder931
FEATURE [Part::MultiFuse] Fusion094
  Shapes = -> [Cut014036,Cut014027]
FEATURE [Part::MultiFuse] Fusion095
  Shapes = -> [Fusion094,Fillet022]
FEATURE [Part::MultiFuse] Fusion096
  Shapes = -> [Cylinder951,Fusion092]
FEATURE [Part::Cut] Cut014037
  Base = -> Fusion095
  Tool = -> Fusion096
FEATURE [Part::Cut] Cut014038
  Base = -> Cut014037
  Tool = -> Fusion083
FEATURE [Part::MultiFuse] Fusion097
  Shapes = -> [Cut014038,Fillet023]
FEATURE [Part::Cut] Cut014039
  Base = -> Fusion097
  Tool = -> Fusion085
FEATURE [Part::MultiFuse] Fusion098
  Shapes = -> [Cut014039,Fusion091]
FEATURE [Part::Cut] Cut014040  label="diff-box-front"
  Base = -> Fusion098
  Tool = -> Fusion067
FEATURE [Part::Chamfer] Chamfer005
  Base = -> Cut014040
  Edges = 1 edges r=2: [Edge6]
FEATURE [Part::Fillet] Fillet025
  Base = -> Chamfer005
  Edges = 1 edges r=3: [Edge18]
FEATURE [Part::Chamfer] Chamfer006
  Base = -> Fillet025
  Edges = 1 edges r=3.49: [Edge24]
FEATURE [Part::MultiFuse] Fusion099
  Shapes = -> [Cylinder085,Cylinder084,Cylinder089,Cylinder090,Cylinder086]
FEATURE [Part::MultiFuse] Fusion100
  Shapes = -> [Cylinder094,Cylinder092,Box002,Fillet009,Fillet005]
FEATURE [Part::Cut] Cut014041
  Base = -> Fusion100
  Tool = -> Fusion099
FEATURE [Part::MultiFuse] Fusion101
  Shapes = -> [Cylinder944,Cylinder097]
FEATURE [Part::Cut] Cut014042
  Base = -> Cut014041
  Tool = -> Fusion101
FEATURE [Part::Cut] Cut014043
  Base = -> Cut014042
  Tool = -> Fusion052
FEATURE [Part::Fillet] Fillet026
  Base = -> Cut014043
  Edges = 2 edges r=1: [Edge78,Edge99]
FEATURE [Part::Chamfer] Chamfer
  Base = -> Fillet026
  Edges = 1 edges r=2.99: [Edge63]
FEATURE [Part::Chamfer] Chamfer007
  Base = -> Chamfer006
  Edges = 2 edges r=1.5: [Edge32,Edge37]
FEATURE [Part::Fillet] Fillet027  label="diff-box-front-01_"
  Base = -> Chamfer007
  Edges = 1 edges r=1.99: [Edge305]
  Placement = pos=(0,0,1) rot=(0,0,1;0rad)
FEATURE [Part::Cylinder] Cylinder953
  Angle = 67
  Height = 3
  Placement = pos=(0,0,-12.5) rot=(0,0,1;2.55691rad)
  Radius = 18
FEATURE [Part::Box] Box559  label="Cube750"
  Height = 3
  Length = 16
  Placement = pos=(-15,-10,-12.5) rot=(0,0,1;0rad)
  Width = 20
FEATURE [Part::Cut] Cut014045
  Base = -> Cylinder953
  Placement = pos=(0,0,1) rot=(0,0,1;0rad)
  Tool = -> Box559
FEATURE [Part::Cylinder] Cylinder954
  Angle = 67
  Height = 2
  Placement = pos=(0,0,-10.5) rot=(0,0,1;2.55691rad)
  Radius = 17
FEATURE [Part::Cut] Cut014046
  Base = -> Cut014045
  Tool = -> Cylinder954
FEATURE [Part::Box] Box560  label="Cube751"
  Height = 5
  Length = 26
  Placement = pos=(-13,-11,-2) rot=(0,0,1;0rad)
  Width = 22
FEATURE [Part::Cylinder] Cylinder955
  Angle = 360
  Height = 15
  Placement = pos=(-10,8,-2) rot=(0,0,1;0rad)
  Radius = 1.25
FEATURE [Part::Cylinder] Cylinder956
  Angle = 360
  Height = 15
  Placement = pos=(-10,-8,-2) rot=(0,0,1;0rad)
  Radius = 1.25
FEATURE [Part::Cylinder] Cylinder957
  Angle = 360
  Height = 15
  Placement = pos=(10,8,-2) rot=(0,0,1;0rad)
  Radius = 1.25
FEATURE [Part::Cylinder] Cylinder958
  Angle = 360
  Height = 15
  Placement = pos=(10,-8,-2) rot=(0,0,1;0rad)
  Radius = 1.25
FEATURE [Part::Cylinder] Cylinder959
  Angle = 360
  Height = 15
  Placement = pos=(0,0,-2) rot=(0,0,1;0rad)
  Radius = 1.6
FEATURE [Part::MultiFuse] Fusion104
  Shapes = -> [Cylinder955,Cylinder958,Cylinder957,Cylinder956]
FEATURE [Part::Cylinder] Cylinder960
  Angle = 360
  Height = 15
  Placement = pos=(-10,8,-2) rot=(0,0,1;0rad)
  Radius = 1.6
FEATURE [Part::Cylinder] Cylinder961
  Angle = 360
  Height = 15
  Placement = pos=(-10,-8,-2) rot=(0,0,1;0rad)
  Radius = 1.6
FEATURE [Part::Cylinder] Cylinder962
  Angle = 360
  Height = 15
  Placement = pos=(10,8,-2) rot=(0,0,1;0rad)
  Radius = 1.6
FEATURE [Part::Cylinder] Cylinder963
  Angle = 360
  Height = 15
  Placement = pos=(10,-8,-2) rot=(0,0,1;0rad)
  Radius = 1.6
FEATURE [Part::MultiFuse] Fusion105
  Shapes = -> [Cylinder960,Cylinder961,Cylinder962,Cylinder963,Cylinder959]
FEATURE [Part::Cut] Cut014048
  Base = -> Cut014011
  Tool = -> Fusion104
FEATURE [Part::Cylinder] Cylinder964
  Angle = 360
  Height = 15
  Placement = pos=(-5,5,-2) rot=(0,0,1;0rad)
  Radius = 2
FEATURE [Part::Cylinder] Cylinder965
  Angle = 360
  Height = 15
  Placement = pos=(5,5,-2) rot=(0,0,1;0rad)
  Radius = 2
FEATURE [Part::Cylinder] Cylinder966
  Angle = 360
  Height = 15
  Placement = pos=(-5,-5,-2) rot=(0,0,1;0rad)
  Radius = 2
FEATURE [Part::Cylinder] Cylinder967
  Angle = 360
  Height = 15
  Placement = pos=(5,-5,-2) rot=(0,0,1;0rad)
  Radius = 2
FEATURE [Part::MultiFuse] Fusion106
  Shapes = -> [Cylinder964,Cylinder965,Cylinder967,Cylinder966]
FEATURE [Part::Cut] Cut014050
  Base = -> Box560
  Tool = -> Fusion105
FEATURE [Part::Cut] Cut014051
  Base = -> Cut014050
  Tool = -> Fusion039
FEATURE [Part::Box] Box561  label="Cube752"
  Height = 5
  Length = 10
  Placement = pos=(7,-2.1,-2) rot=(0,0,1;0rad)
  Width = 4.2
FEATURE [Part::Box] Box562  label="Cube753"
  Height = 5
  Length = 10
  Placement = pos=(-17,-2.1,-2) rot=(0,0,1;0rad)
  Width = 4.2
FEATURE [Part::Box] Box563  label="Cube754"
  Height = 5
  Length = 4.2
  Placement = pos=(-2.1,7,-2) rot=(0,0,1;0rad)
  Width = 10
FEATURE [Part::Box] Box564  label="Cube755"
  Height = 5
  Length = 4.2
  Placement = pos=(-2.1,-17,-2) rot=(0,0,1;0rad)
  Width = 10
FEATURE [Part::MultiFuse] Fusion107
  Shapes = -> [Box561,Box564,Box562,Box563]
FEATURE [Part::Cylinder] Cylinder968
  Angle = 360
  Height = 15
  Placement = pos=(7,0,0) rot=(0,0,1;0rad)
  Radius = 2.1
FEATURE [Part::Cylinder] Cylinder969
  Angle = 360
  Height = 15
  Placement = pos=(-7,0,0) rot=(0,0,1;0rad)
  Radius = 2.1
FEATURE [Part::MultiFuse] Fusion108
  Shapes = -> [Cylinder969,Cylinder968]
FEATURE [Part::Cylinder] Cylinder970
  Angle = 360
  Height = 15
  Placement = pos=(7,0,0) rot=(0,0,1;0rad)
  Radius = 2.1
FEATURE [Part::Cylinder] Cylinder971
  Angle = 360
  Height = 15
  Placement = pos=(-7,0,0) rot=(0,0,1;0rad)
  Radius = 2.1
FEATURE [Part::MultiFuse] Fusion109
  Placement = pos=(0,0,0) rot=(0,0,1;1.5708rad)
  Shapes = -> [Cylinder971,Cylinder970]
FEATURE [Part::MultiFuse] Fusion110
  Placement = pos=(0,0,-14) rot=(0,0,1;0rad)
  Shapes = -> [Fusion109,Fusion108]
FEATURE [Part::Cut] Cut014053
  Base = -> Cut014048
  Tool = -> Fusion106
FEATURE [Part::Cut] Cut014054  label="diff_lock_planetary_inf_HOLES"
  Base = -> Cut014053
  Tool = -> Fusion110
FEATURE [Part::Cylinder] Cylinder972  label="Cylinder1035"
  Angle = 360
  Height = 4.2
  Radius = 8.75
FEATURE [Part::Cylinder] Cylinder973  label="Cylinder1036"
  Angle = 360
  Height = 3.5
  Placement = pos=(0,0,-3.5) rot=(0,0,1;0rad)
  Radius = 4.45
FEATURE [Part::MultiFuse] Fusion111
  Shapes = -> [Cylinder973,Cylinder972]
FEATURE [Part::Cylinder] Cylinder974
  Angle = 360
  Height = 3.5
  Placement = pos=(0,0,-3.5) rot=(0,0,1;0rad)
  Radius = 4.6
FEATURE [Part::Cut] Cut014055
  Base = -> Cut014051
  Placement = pos=(0,0,-3) rot=(0,0,1;0rad)
  Tool = -> Fusion107
FEATURE [Part::Cut] Cut014056  label="diff_lock_planetary_sup_HOLES"
  Base = -> Cut014055
  Tool = -> Cylinder974
FEATURE [Part::Chamfer] Chamfer008  label="planetary-gear"
  Base = -> Fusion111
  Edges = 1 edges r=3.5: [Edge5]
FEATURE [Part::Cylinder] Cylinder975  label="Cylinder1037"
  Angle = 360
  Height = 20
  Placement = pos=(19.5,30,-7.5) rot=(1,0,0;1.5708rad)
  Radius = 1.6
FEATURE [Part::Cylinder] Cylinder976  label="Cylinder1038"
  Angle = 360
  Height = 20
  Placement = pos=(19.5,30,0.5) rot=(1,0,0;1.5708rad)
  Radius = 1.6
FEATURE [Part::MultiFuse] Fusion112
  Placement = pos=(0,-43,-1) rot=(0,0,1;0rad)
  Shapes = -> [Cylinder975,Cylinder976]
FEATURE [Part::Box] Box491  label="Cube693"
  Height = 21
  Length = 16
  Placement = pos=(128,50.5,-21.5) rot=(0,0,1;0rad)
  Width = 3
FEATURE [Part::Box] Box492  label="Cube694"
  Height = 3
  Length = 16
  Placement = pos=(128,50.5,-24.5) rot=(0,0,1;0rad)
  Width = 10
FEATURE [Part::Box] Box493  label="Cube695"
  Height = 3
  Length = 16
  Placement = pos=(128,50.5,-0.5) rot=(0,0,1;0rad)
  Width = 10
FEATURE [Part::MultiFuse] Fusion493
  Placement = pos=(30.5,-83.5,131.5) rot=(0,1,0;1.5708rad)
  Shapes = -> [Box491,Box493,Box492]
FEATURE [Part::Cut] Cut014057  label="diff-box-mount-HOLES"
  Base = -> Fusion493
  Tool = -> Fusion112
FEATURE [Part::Box] Box565  label="Cube756"
  Height = 18
  Length = 10
  Placement = pos=(11,-6.5,-10.5) rot=(0,0,1;0rad)
  Width = 13
FEATURE [Part::Cut] Cut014058
  Base = -> Chamfer
  Tool = -> Box565
FEATURE [Part::MultiFuse] Fusion494
  Shapes = -> [Cut014058,Cut014019]
FEATURE [Part::MultiFuse] Fusion495
  Shapes = -> [Fusion494,Cut014046]
FEATURE [Part::Fillet] Fillet028
  Base = -> Fusion495
  Edges = 2 edges r=3: [Edge1,Edge16]
FEATURE [Part::Cut] Cut014059  label="diff-box-rear-01"
  Base = -> Fillet028
  Tool = -> Fusion086
FEATURE [Part::Chamfer] Chamfer009  label="diff-box-geared-01"
  Base = -> Cut014008
  Edges = 39 edges r=1: [Edge16,Edge30,Edge44,Edge58,Edge72,Edge86,Edge100,Edge114,Edge128,Edge142,Edge156,Edge170,Edge184,Edge198,Edge212,Edge226,Edge240,Edge254,Edge268,Edge282,Edge296,Edge310,Edge324,Edge338,Edge352,Edge366,Edge380,Edge394,Edge408,Edge422,Edge436,Edge450,Edge464,Edge478,Edge492,Edge506,Edge520,Edge534,+1 more]
FEATURE [Part::Chamfer] Chamfer010  label="diff-box-front-01"
  Base = -> Fillet027
  Edges = 1 edges r=1.5: [Edge138]
